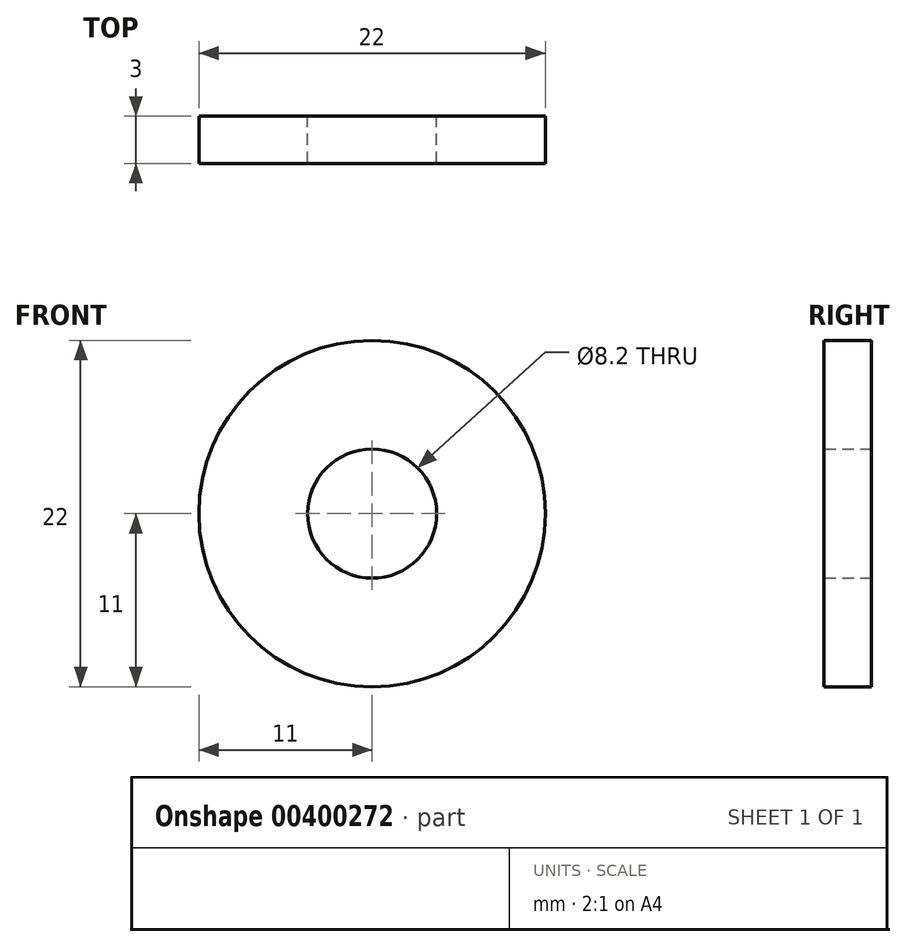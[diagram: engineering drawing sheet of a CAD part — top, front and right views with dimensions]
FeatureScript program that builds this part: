
annotation { "Feature Type Name" : "Feature", "Feature Type Description" : "" }
export const myFeature = defineFeature(function(context is Context, id is Id, definition is map)
    precondition{}
    {
        {
            var Q0;
            Q0=qCreatedBy(makeId("Front.planeOp"),FACE);
            var sketch = newSketch(context, id + "F0", { "sketchPlane" : qUnion([Q0])});
            skCircle(sketch, "E0", {"center": v(0, 0) * mm, "radius": 11 * mm});
            skCircle(sketch, "E1", {"center": v(0, 0) * mm, "radius": 4.1 * mm});
            skSolve(sketch);
        }
        {
            var Q0;
            Q0=makeQuery(id+"F0.imprint","IMPRINT",FACE,{"disambiguationData":[TD([[makeQuery(id+"F0.imprint","IMPRINT",EDGE,{"derivedFrom":sQuery(id+"F0.wireOp",EDGE,"E0")}),1.0]])]});
            extrude(context, id + "F1", {"entities" : qUnion([Q0]), "depth" : 3 * mm, "offsetDistance" : 25 * mm});
        }
    });
